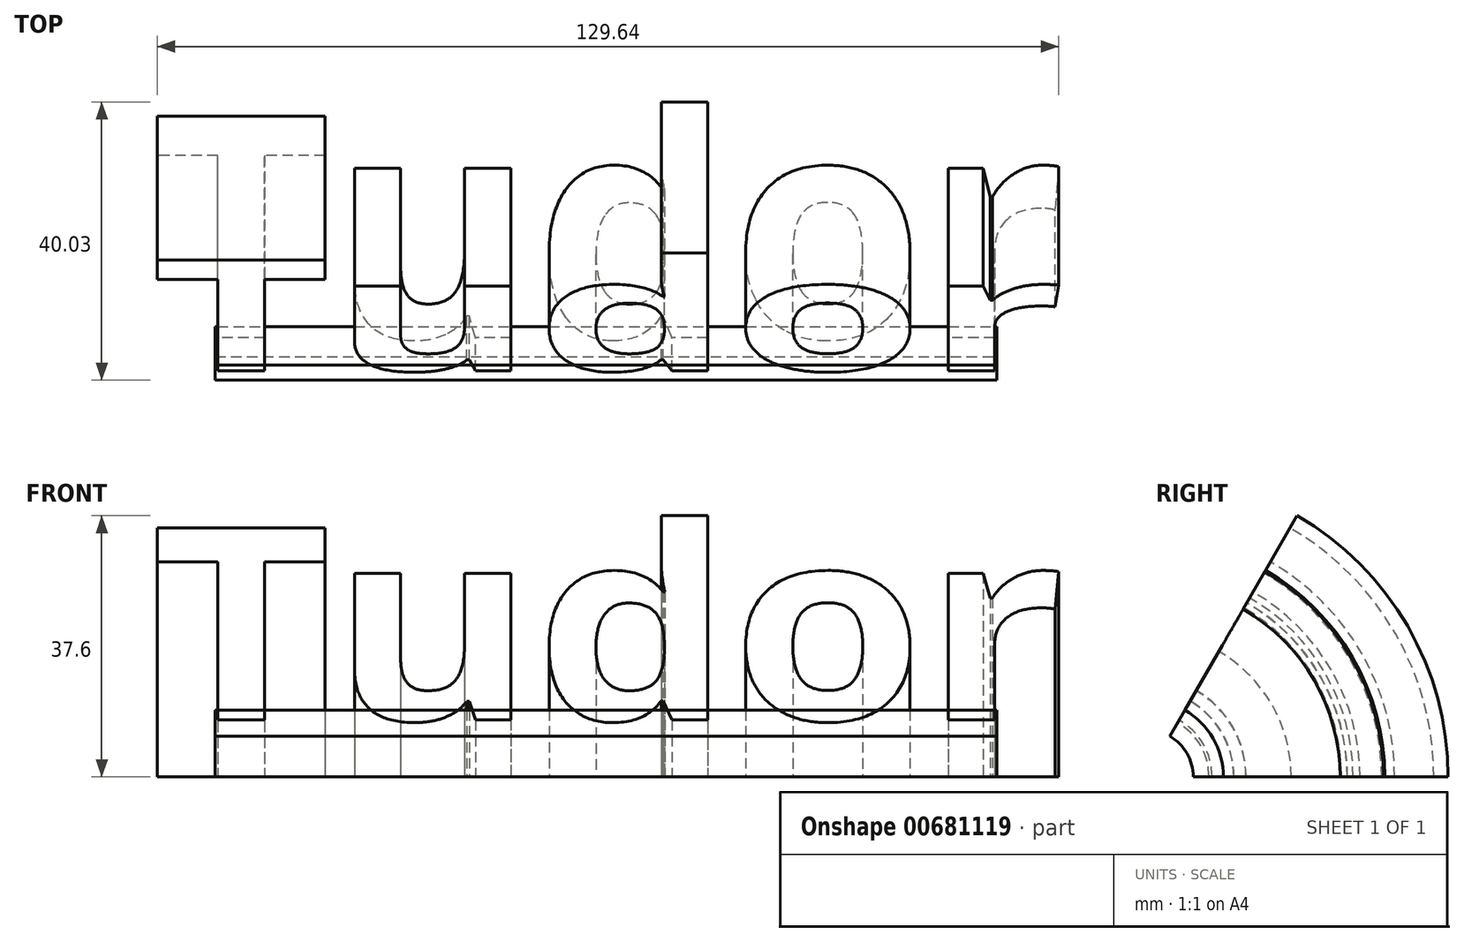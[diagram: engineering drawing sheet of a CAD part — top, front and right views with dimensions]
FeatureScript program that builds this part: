
annotation { "Feature Type Name" : "Feature", "Feature Type Description" : "" }
export const myFeature = defineFeature(function(context is Context, id is Id, definition is map)
    precondition{}
    {
        {
            var Q0;
            Q0=qCreatedBy(makeId("Top.planeOp"),FACE);
            var sketch = newSketch(context, id + "F0", { "sketchPlane" : qUnion([Q0])});
            skText(sketch, "E0", { "text": "Tudor", "fontName": "OpenSans-Bold.ttf"});
            const initialGuessF0  = {"E0": [-0.07535, -0.00858, 1, 0, 0.03217]};
            skSetInitialGuess(sketch, initialGuessF0);
            skSolve(sketch);
        }
        {
            var Q0;
            Q0=qCreatedBy(makeId("Top.planeOp"),FACE);
            var sketch = newSketch(context, id + "F1", { "sketchPlane" : qUnion([Q0])});
            skLineSegment(sketch, "E1.bottom", {"start": v(-66.16, -6.96) * mm, "end": v(46.29, -6.96) * mm});
            skLineSegment(sketch, "E1.top", {"start": v(-66.16, -11.29) * mm, "end": v(46.29, -11.29) * mm});
            skLineSegment(sketch, "E1.left", {"start": v(-66.16, -6.96) * mm, "end": v(-66.16, -11.29) * mm});
            skLineSegment(sketch, "E1.right", {"start": v(46.29, -6.96) * mm, "end": v(46.29, -11.29) * mm});
            skSolve(sketch);
        }
        {
            var Q0;
            Q0=qCreatedBy(makeId("Top.planeOp"),FACE);
            var sketch = newSketch(context, id + "F2", { "sketchPlane" : qUnion([Q0])});
            skLineSegment(sketch, "E2", {"start": v(-82.1, -18.04) * mm, "end": v(81.43, -18.04) * mm});
            skSolve(sketch);
        }
        {
            var Q0;
            Q0 = qSketchRegion(id + "F0", true);
            var Q1;
            Q1=makeQuery(id+"F1.imprint","IMPRINT",FACE,{"disambiguationData":[TD([[makeQuery(id+"F1.imprint","IMPRINT",EDGE,{"derivedFrom":sQuery(id+"F1.wireOp",EDGE,"E1.bottom")}),-1.0]])]});
            var Q2;
            Q2=sQuery(id+"F2.wireOp",EDGE,"E2");
            revolve(context, id + "F3", {"entities" : qUnion([Q0, Q1]), "axis" : qUnion([Q2]), "revolveType" : RevolveType.ONE_DIRECTION, "angle" : 60 * degree});
        }
    });
